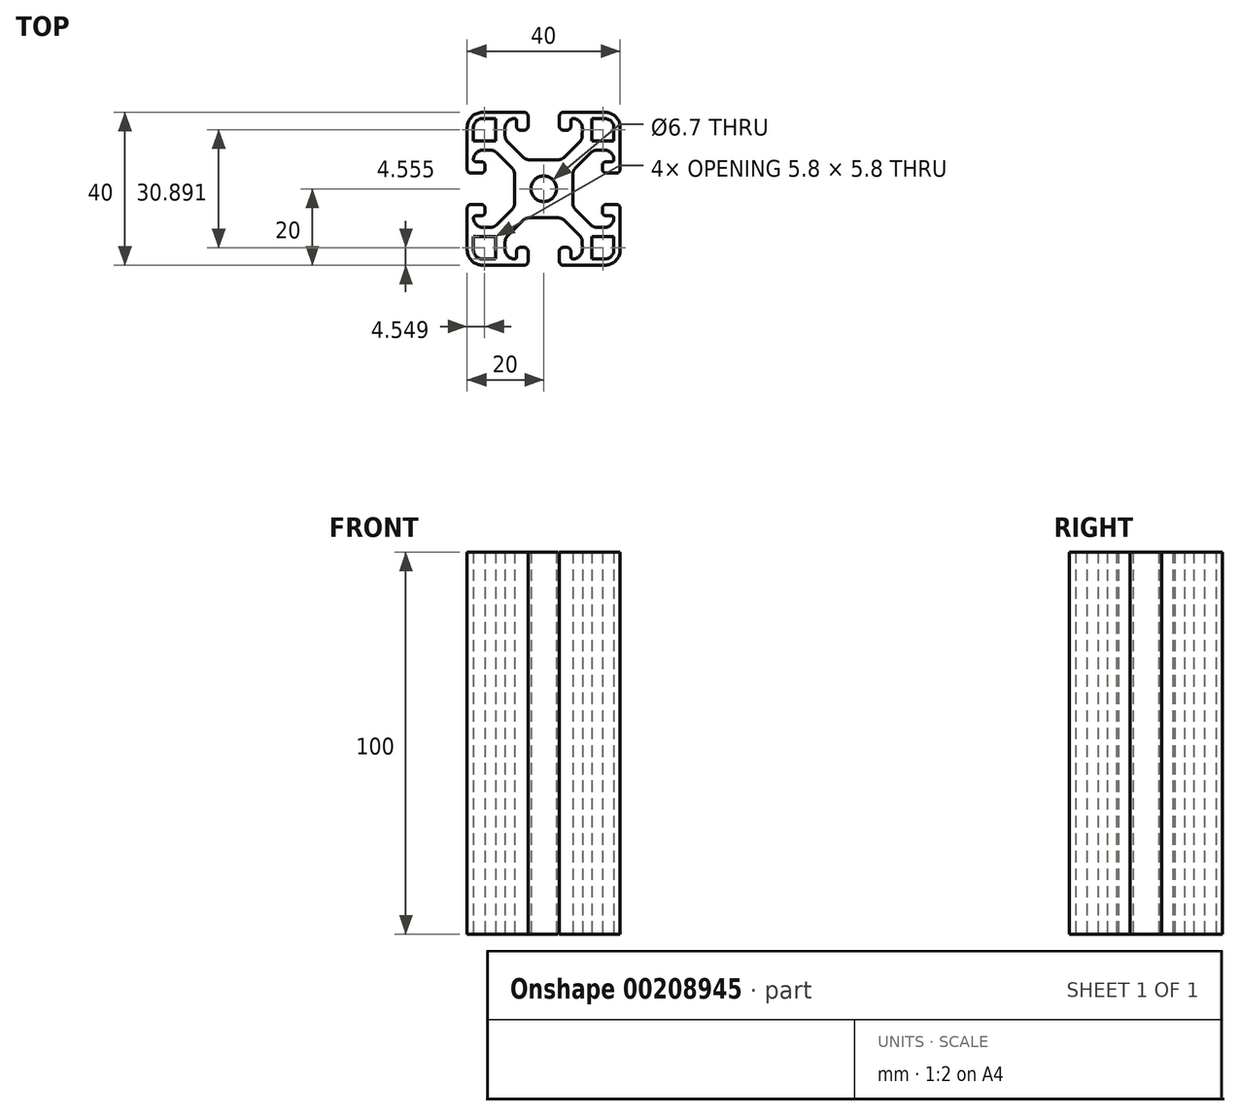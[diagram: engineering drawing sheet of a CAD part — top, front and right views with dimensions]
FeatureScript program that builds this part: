
annotation { "Feature Type Name" : "Feature", "Feature Type Description" : "" }
export const myFeature = defineFeature(function(context is Context, id is Id, definition is map)
    precondition{}
    {
        {
            var Q0;
            Q0=qCreatedBy(makeId("Top.planeOp"),FACE);
            var sketch = newSketch(context, id + "F0", { "sketchPlane" : qUnion([Q0])});
            skCircle(sketch, "E0", {"center": v(0, 0) * mm, "radius": 3.35 * mm});
            skPoint(sketch, "E1.rect.middle", {"position": v(13.8, 0) * mm});
            skPoint(sketch, "E2.newPointA", {"position": v(20, 20) * mm});
            skPoint(sketch, "E2.newPointB", {"position": v(20, -4.1) * mm});
            skArc(sketch, "E2.filletArc", {"start": v(20, -5.1) * mm, "mid": v(19.7, -4.4) * mm, "end": v(19, -4.1) * mm});
            skPoint(sketch, "E3.visualSharp", {"position": v(20, -20) * mm});
            skLineSegment(sketch, "E4", {"start": v(15.35, -5.1) * mm, "end": v(15.35, -6.1) * mm});
            skLineSegment(sketch, "E5", {"start": v(16.35, -7.1) * mm, "end": v(17.85, -7.1) * mm});
            skLineSegment(sketch, "E6", {"start": v(18.35, -7.6) * mm, "end": v(18.35, -7.6) * mm});
            skLineSegment(sketch, "E7", {"start": v(15.85, -10.1) * mm, "end": v(14, -10.1) * mm});
            skPoint(sketch, "E8.visualSharp", {"position": v(15.35, -4.1) * mm});
            skArc(sketch, "E8.filletArc", {"start": v(16.35, -4.1) * mm, "mid": v(15.64, -4.4) * mm, "end": v(15.35, -5.1) * mm});
            skPoint(sketch, "E9.visualSharp", {"position": v(15.35, -7.1) * mm});
            skArc(sketch, "E9.filletArc", {"start": v(15.35, -6.1) * mm, "mid": v(15.64, -6.8) * mm, "end": v(16.35, -7.1) * mm});
            skPoint(sketch, "E10.visualSharp", {"position": v(18.35, -7.1) * mm});
            skArc(sketch, "E10.filletArc", {"start": v(18.35, -7.6) * mm, "mid": v(18.2, -7.25) * mm, "end": v(17.85, -7.1) * mm});
            skPoint(sketch, "E11.visualSharp", {"position": v(18.35, -10.1) * mm});
            skArc(sketch, "E11.filletArc", {"start": v(15.85, -10.1) * mm, "mid": v(17.62, -9.37) * mm, "end": v(18.35, -7.6) * mm});
            skLineSegment(sketch, "E12", {"start": v(12.23, -9.37) * mm, "end": v(8.33, -5.48) * mm});
            skPoint(sketch, "E13.newPointA", {"position": v(7.6, -10.1) * mm});
            skArc(sketch, "E13.filletArc", {"start": v(12.23, -9.37) * mm, "mid": v(13.04, -9.9) * mm, "end": v(14, -10.1) * mm});
            skArc(sketch, "E14.filletArc", {"start": v(7.6, -3.7) * mm, "mid": v(7.8, -4.66) * mm, "end": v(8.33, -5.48) * mm});
            skArc(sketch, "E15.MirrorCS", {"start": v(9.37, -12.22) * mm, "mid": v(9.91, -13.03) * mm, "end": v(10.1, -13.99) * mm});
            skArc(sketch, "E16.MirrorCS", {"start": v(10.1, -15.85) * mm, "mid": v(9.37, -17.61) * mm, "end": v(7.6, -18.35) * mm});
            skLineSegment(sketch, "E17.MirrorCS", {"start": v(7.1, -16.35) * mm, "end": v(7.1, -17.85) * mm});
            skArc(sketch, "E18.MirrorCS", {"start": v(3.71, -7.6) * mm, "mid": v(4.67, -7.79) * mm, "end": v(5.48, -8.33) * mm});
            skArc(sketch, "E19.MirrorCS", {"start": v(5.1, -20) * mm, "mid": v(4.4, -19.7) * mm, "end": v(4.1, -19) * mm});
            skLineSegment(sketch, "E20.MirrorCS", {"start": v(10.1, -15.85) * mm, "end": v(10.1, -13.99) * mm});
            skArc(sketch, "E21.MirrorCS", {"start": v(6.1, -15.35) * mm, "mid": v(6.81, -15.64) * mm, "end": v(7.1, -16.35) * mm});
            skLineSegment(sketch, "E22.MirrorCS", {"start": v(9.37, -12.22) * mm, "end": v(5.48, -8.33) * mm});
            skLineSegment(sketch, "E23.MirrorCS", {"start": v(5.1, -15.35) * mm, "end": v(6.1, -15.35) * mm});
            skArc(sketch, "E24.MirrorCS", {"start": v(7.6, -18.35) * mm, "mid": v(7.25, -18.2) * mm, "end": v(7.1, -17.85) * mm});
            skLineSegment(sketch, "E25.MirrorCS", {"start": v(7.6, -18.35) * mm, "end": v(7.6, -18.35) * mm});
            skPoint(sketch, "E26.MirrorP", {"position": v(0, -13.8) * mm});
            skPoint(sketch, "E27.MirrorP", {"position": v(4.1, -15.35) * mm});
            skPoint(sketch, "E28.MirrorP", {"position": v(7.1, -15.35) * mm});
            skPoint(sketch, "E29.MirrorP", {"position": v(10.1, -18.35) * mm});
            skPoint(sketch, "E30.MirrorP", {"position": v(10.1, -7.6) * mm});
            skPoint(sketch, "E31.MirrorP", {"position": v(7.1, -18.35) * mm});
            skArc(sketch, "E32.MirrorCS", {"start": v(4.1, -16.35) * mm, "mid": v(4.4, -15.64) * mm, "end": v(5.1, -15.35) * mm});
            skLineSegment(sketch, "E33.bottom", {"start": v(16, -18.35) * mm, "end": v(12.55, -18.35) * mm});
            skLineSegment(sketch, "E33.top", {"start": v(18.35, -12.54) * mm, "end": v(12.55, -12.54) * mm});
            skLineSegment(sketch, "E33.left", {"start": v(18.35, -16) * mm, "end": v(18.35, -12.54) * mm});
            skLineSegment(sketch, "E33.right", {"start": v(12.55, -18.35) * mm, "end": v(12.55, -12.54) * mm});
            skPoint(sketch, "E34.visualSharp", {"position": v(18.35, -18.35) * mm});
            skArc(sketch, "E34.filletArc", {"start": v(16, -18.35) * mm, "mid": v(17.66, -17.66) * mm, "end": v(18.35, -16) * mm});
            skLineSegment(sketch, "E35.MirrorCS", {"start": v(-18.35, -7.6) * mm, "end": v(-18.35, -7.6) * mm});
            skPoint(sketch, "E36.MirrorP", {"position": v(-18.35, -10.1) * mm});
            skPoint(sketch, "E37.MirrorP", {"position": v(-18.35, -18.35) * mm});
            skArc(sketch, "E38.MirrorCS", {"start": v(-15.85, -10.1) * mm, "mid": v(-17.62, -9.37) * mm, "end": v(-18.35, -7.6) * mm});
            skPoint(sketch, "E39.MirrorP", {"position": v(-13.8, 0) * mm});
            skArc(sketch, "E40.MirrorCS", {"start": v(-6.1, -15.35) * mm, "mid": v(-6.81, -15.64) * mm, "end": v(-7.1, -16.35) * mm});
            skLineSegment(sketch, "E41.MirrorCS", {"start": v(-16.35, -7.1) * mm, "end": v(-17.85, -7.1) * mm});
            skLineSegment(sketch, "E42.MirrorCS", {"start": v(-15.85, -10.1) * mm, "end": v(-14, -10.1) * mm});
            skPoint(sketch, "E43.MirrorP", {"position": v(-18.35, -7.1) * mm});
            skArc(sketch, "E44.MirrorCS", {"start": v(-20, -5.1) * mm, "mid": v(-19.7, -4.4) * mm, "end": v(-19, -4.1) * mm});
            skLineSegment(sketch, "E45.MirrorCS", {"start": v(-15.35, -5.1) * mm, "end": v(-15.35, -6.1) * mm});
            skPoint(sketch, "E46.MirrorP", {"position": v(-15.35, -4.1) * mm});
            skLineSegment(sketch, "E47.MirrorCS", {"start": v(-7.1, -16.35) * mm, "end": v(-7.1, -17.85) * mm});
            skPoint(sketch, "E48.MirrorP", {"position": v(-20, -20) * mm});
            skPoint(sketch, "E49.MirrorP", {"position": v(-15.35, -7.1) * mm});
            skPoint(sketch, "E50.MirrorP", {"position": v(-20, -4.1) * mm});
            skLineSegment(sketch, "E51.MirrorCS", {"start": v(-7.6, -18.35) * mm, "end": v(-7.6, -18.35) * mm});
            skPoint(sketch, "E52.MirrorP", {"position": v(-10.1, -7.6) * mm});
            skArc(sketch, "E53.MirrorCS", {"start": v(-7.6, -18.35) * mm, "mid": v(-7.25, -18.2) * mm, "end": v(-7.1, -17.85) * mm});
            skLineSegment(sketch, "E54.MirrorCS", {"start": v(-18.35, -16) * mm, "end": v(-18.35, -12.54) * mm});
            skArc(sketch, "E55.MirrorCS", {"start": v(-15.35, -6.1) * mm, "mid": v(-15.64, -6.8) * mm, "end": v(-16.35, -7.1) * mm});
            skArc(sketch, "E56.MirrorCS", {"start": v(-18.35, -7.6) * mm, "mid": v(-18.2, -7.25) * mm, "end": v(-17.85, -7.1) * mm});
            skPoint(sketch, "E57.MirrorP", {"position": v(-7.1, -15.35) * mm});
            skPoint(sketch, "E58.MirrorP", {"position": v(-7.6, -10.1) * mm});
            skLineSegment(sketch, "E59.MirrorCS", {"start": v(-12.55, -18.35) * mm, "end": v(-12.55, -12.54) * mm});
            skArc(sketch, "E60.MirrorCS", {"start": v(-16.35, -4.1) * mm, "mid": v(-15.64, -4.4) * mm, "end": v(-15.35, -5.1) * mm});
            skArc(sketch, "E61.MirrorCS", {"start": v(-12.23, -9.37) * mm, "mid": v(-13.04, -9.9) * mm, "end": v(-14, -10.1) * mm});
            skArc(sketch, "E62.MirrorCS", {"start": v(-9.37, -12.22) * mm, "mid": v(-9.91, -13.03) * mm, "end": v(-10.1, -13.99) * mm});
            skPoint(sketch, "E63.MirrorP", {"position": v(-4.1, -15.35) * mm});
            skLineSegment(sketch, "E64.MirrorCS", {"start": v(-18.35, -12.54) * mm, "end": v(-12.55, -12.54) * mm});
            skArc(sketch, "E65.MirrorCS", {"start": v(-7.6, -3.7) * mm, "mid": v(-7.8, -4.66) * mm, "end": v(-8.33, -5.48) * mm});
            skPoint(sketch, "E66.MirrorP", {"position": v(-7.1, -18.35) * mm});
            skArc(sketch, "E67.MirrorCS", {"start": v(-4.1, -16.35) * mm, "mid": v(-4.4, -15.64) * mm, "end": v(-5.1, -15.35) * mm});
            skLineSegment(sketch, "E68.MirrorCS", {"start": v(-9.37, -12.22) * mm, "end": v(-5.48, -8.33) * mm});
            skLineSegment(sketch, "E69.MirrorCS", {"start": v(-10.1, -15.85) * mm, "end": v(-10.1, -13.99) * mm});
            skArc(sketch, "E70.MirrorCS", {"start": v(-5.1, -20) * mm, "mid": v(-4.4, -19.7) * mm, "end": v(-4.1, -19) * mm});
            skPoint(sketch, "E71.MirrorP", {"position": v(-10.1, -18.35) * mm});
            skPoint(sketch, "E72.MirrorP", {"position": v(-4.1, -20) * mm});
            skArc(sketch, "E73.MirrorCS", {"start": v(-16, -18.35) * mm, "mid": v(-17.66, -17.66) * mm, "end": v(-18.35, -16) * mm});
            skLineSegment(sketch, "E74.MirrorCS", {"start": v(-16, -18.35) * mm, "end": v(-12.55, -18.35) * mm});
            skArc(sketch, "E75.MirrorCS", {"start": v(-10.1, -15.85) * mm, "mid": v(-9.37, -17.61) * mm, "end": v(-7.6, -18.35) * mm});
            skArc(sketch, "E76.MirrorCS", {"start": v(-3.71, -7.6) * mm, "mid": v(-4.67, -7.79) * mm, "end": v(-5.48, -8.33) * mm});
            skLineSegment(sketch, "E77.MirrorCS", {"start": v(-5.1, -15.35) * mm, "end": v(-6.1, -15.35) * mm});
            skLineSegment(sketch, "E78.MirrorCS", {"start": v(-12.23, -9.37) * mm, "end": v(-8.33, -5.48) * mm});
            skLineSegment(sketch, "E79.MirrorCS", {"start": v(-12.23, 9.37) * mm, "end": v(-8.33, 5.48) * mm});
            skArc(sketch, "E80.MirrorCS", {"start": v(16, 18.35) * mm, "mid": v(17.66, 17.66) * mm, "end": v(18.35, 16) * mm});
            skArc(sketch, "E81.MirrorCS", {"start": v(10.1, 15.85) * mm, "mid": v(9.37, 17.61) * mm, "end": v(7.6, 18.35) * mm});
            skLineSegment(sketch, "E82.MirrorCS", {"start": v(-15.35, 5.1) * mm, "end": v(-15.35, 6.1) * mm});
            skLineSegment(sketch, "E83.MirrorCS", {"start": v(5.1, 15.35) * mm, "end": v(6.1, 15.35) * mm});
            skArc(sketch, "E84.MirrorCS", {"start": v(-6.1, 15.35) * mm, "mid": v(-6.81, 15.64) * mm, "end": v(-7.1, 16.35) * mm});
            skLineSegment(sketch, "E85.MirrorCS", {"start": v(7.1, 16.35) * mm, "end": v(7.1, 17.85) * mm});
            skLineSegment(sketch, "E86.MirrorCS", {"start": v(-12.55, 18.35) * mm, "end": v(-12.55, 12.54) * mm});
            skLineSegment(sketch, "E87.MirrorCS", {"start": v(12.23, 9.37) * mm, "end": v(8.33, 5.48) * mm});
            skLineSegment(sketch, "E88.MirrorCS", {"start": v(-7.1, 16.35) * mm, "end": v(-7.1, 17.85) * mm});
            skArc(sketch, "E89.MirrorCS", {"start": v(-12.23, 9.37) * mm, "mid": v(-13.04, 9.9) * mm, "end": v(-14, 10.1) * mm});
            skArc(sketch, "E90.MirrorCS", {"start": v(-3.71, 7.6) * mm, "mid": v(-4.67, 7.79) * mm, "end": v(-5.48, 8.33) * mm});
            skArc(sketch, "E91.MirrorCS", {"start": v(12.23, 9.37) * mm, "mid": v(13.04, 9.9) * mm, "end": v(14, 10.1) * mm});
            skArc(sketch, "E92.MirrorCS", {"start": v(7.6, 18.35) * mm, "mid": v(7.25, 18.2) * mm, "end": v(7.1, 17.85) * mm});
            skArc(sketch, "E93.MirrorCS", {"start": v(5.1, 20) * mm, "mid": v(4.4, 19.7) * mm, "end": v(4.1, 19) * mm});
            skArc(sketch, "E94.MirrorCS", {"start": v(-4.1, 16.35) * mm, "mid": v(-4.4, 15.64) * mm, "end": v(-5.1, 15.35) * mm});
            skLineSegment(sketch, "E95.MirrorCS", {"start": v(-5.1, 15.35) * mm, "end": v(-6.1, 15.35) * mm});
            skArc(sketch, "E96.MirrorCS", {"start": v(3.71, 7.6) * mm, "mid": v(4.67, 7.79) * mm, "end": v(5.48, 8.33) * mm});
            skArc(sketch, "E97.MirrorCS", {"start": v(4.1, 16.35) * mm, "mid": v(4.4, 15.64) * mm, "end": v(5.1, 15.35) * mm});
            skArc(sketch, "E98.MirrorCS", {"start": v(-7.6, 18.35) * mm, "mid": v(-7.25, 18.2) * mm, "end": v(-7.1, 17.85) * mm});
            skArc(sketch, "E99.MirrorCS", {"start": v(7.6, 3.7) * mm, "mid": v(7.8, 4.66) * mm, "end": v(8.33, 5.48) * mm});
            skArc(sketch, "E100.MirrorCS", {"start": v(-16.35, 4.1) * mm, "mid": v(-15.64, 4.4) * mm, "end": v(-15.35, 5.1) * mm});
            skArc(sketch, "E101.MirrorCS", {"start": v(-16, 18.35) * mm, "mid": v(-17.66, 17.66) * mm, "end": v(-18.35, 16) * mm});
            skArc(sketch, "E102.MirrorCS", {"start": v(-9.37, 12.22) * mm, "mid": v(-9.91, 13.03) * mm, "end": v(-10.1, 13.99) * mm});
            skArc(sketch, "E103.MirrorCS", {"start": v(-10.1, 15.85) * mm, "mid": v(-9.37, 17.61) * mm, "end": v(-7.6, 18.35) * mm});
            skArc(sketch, "E104.MirrorCS", {"start": v(-15.85, 10.1) * mm, "mid": v(-17.62, 9.37) * mm, "end": v(-18.35, 7.6) * mm});
            skLineSegment(sketch, "E105.MirrorCS", {"start": v(16, 18.35) * mm, "end": v(12.55, 18.35) * mm});
            skLineSegment(sketch, "E106.MirrorCS", {"start": v(-15.85, 10.1) * mm, "end": v(-14, 10.1) * mm});
            skArc(sketch, "E107.MirrorCS", {"start": v(-7.6, 3.7) * mm, "mid": v(-7.8, 4.66) * mm, "end": v(-8.33, 5.48) * mm});
            skLineSegment(sketch, "E108.MirrorCS", {"start": v(-16, 18.35) * mm, "end": v(-12.55, 18.35) * mm});
            skLineSegment(sketch, "E109.MirrorCS", {"start": v(-16.35, 7.1) * mm, "end": v(-17.85, 7.1) * mm});
            skLineSegment(sketch, "E110.MirrorCS", {"start": v(15.85, 10.1) * mm, "end": v(14, 10.1) * mm});
            skLineSegment(sketch, "E111.MirrorCS", {"start": v(10.1, 15.85) * mm, "end": v(10.1, 13.99) * mm});
            skLineSegment(sketch, "E112.MirrorCS", {"start": v(-18.35, 16) * mm, "end": v(-18.35, 12.54) * mm});
            skArc(sketch, "E113.MirrorCS", {"start": v(16.35, 4.1) * mm, "mid": v(15.64, 4.4) * mm, "end": v(15.35, 5.1) * mm});
            skLineSegment(sketch, "E114.MirrorCS", {"start": v(15.35, 5.1) * mm, "end": v(15.35, 6.1) * mm});
            skLineSegment(sketch, "E115.MirrorCS", {"start": v(18.35, 12.54) * mm, "end": v(12.55, 12.54) * mm});
            skArc(sketch, "E116.MirrorCS", {"start": v(20, 5.1) * mm, "mid": v(19.7, 4.4) * mm, "end": v(19, 4.1) * mm});
            skArc(sketch, "E117.MirrorCS", {"start": v(9.37, 12.22) * mm, "mid": v(9.91, 13.03) * mm, "end": v(10.1, 13.99) * mm});
            skLineSegment(sketch, "E118.MirrorCS", {"start": v(-18.35, 12.54) * mm, "end": v(-12.55, 12.54) * mm});
            skArc(sketch, "E119.MirrorCS", {"start": v(15.35, 6.1) * mm, "mid": v(15.64, 6.8) * mm, "end": v(16.35, 7.1) * mm});
            skLineSegment(sketch, "E120.MirrorCS", {"start": v(-9.37, 12.22) * mm, "end": v(-5.48, 8.33) * mm});
            skLineSegment(sketch, "E121.MirrorCS", {"start": v(18.35, 16) * mm, "end": v(18.35, 12.54) * mm});
            skArc(sketch, "E122.MirrorCS", {"start": v(-15.35, 6.1) * mm, "mid": v(-15.64, 6.8) * mm, "end": v(-16.35, 7.1) * mm});
            skLineSegment(sketch, "E123.MirrorCS", {"start": v(18.35, 7.6) * mm, "end": v(18.35, 7.6) * mm});
            skPoint(sketch, "E124.MirrorP", {"position": v(0, 13.8) * mm});
            skLineSegment(sketch, "E125.MirrorCS", {"start": v(7.6, 18.35) * mm, "end": v(7.6, 18.35) * mm});
            skPoint(sketch, "E126.MirrorP", {"position": v(18.35, 10.1) * mm});
            skPoint(sketch, "E127.MirrorP", {"position": v(10.1, 7.6) * mm});
            skPoint(sketch, "E128.MirrorP", {"position": v(20, 4.1) * mm});
            skArc(sketch, "E129.MirrorCS", {"start": v(18.35, 7.6) * mm, "mid": v(18.2, 7.25) * mm, "end": v(17.85, 7.1) * mm});
            skPoint(sketch, "E130.MirrorP", {"position": v(10.1, 18.35) * mm});
            skPoint(sketch, "E131.MirrorP", {"position": v(18.35, 7.1) * mm});
            skPoint(sketch, "E132.MirrorP", {"position": v(7.1, 15.35) * mm});
            skPoint(sketch, "E133.MirrorP", {"position": v(4.1, 15.35) * mm});
            skPoint(sketch, "E134.MirrorP", {"position": v(15.35, 4.1) * mm});
            skPoint(sketch, "E135.MirrorP", {"position": v(7.6, 10.1) * mm});
            skPoint(sketch, "E136.MirrorP", {"position": v(7.1, 18.35) * mm});
            skPoint(sketch, "E137.MirrorP", {"position": v(15.35, 7.1) * mm});
            skPoint(sketch, "E138.MirrorP", {"position": v(4.1, 20) * mm});
            skPoint(sketch, "E139.MirrorP", {"position": v(18.35, 18.35) * mm});
            skArc(sketch, "E140.MirrorCS", {"start": v(15.85, 10.1) * mm, "mid": v(17.62, 9.37) * mm, "end": v(18.35, 7.6) * mm});
            skPoint(sketch, "E141.MirrorP", {"position": v(-4.1, 20) * mm});
            skLineSegment(sketch, "E142.MirrorCS", {"start": v(12.55, 18.35) * mm, "end": v(12.55, 12.54) * mm});
            skArc(sketch, "E143.MirrorCS", {"start": v(6.1, 15.35) * mm, "mid": v(6.81, 15.64) * mm, "end": v(7.1, 16.35) * mm});
            skLineSegment(sketch, "E144.MirrorCS", {"start": v(-10.1, 15.85) * mm, "end": v(-10.1, 13.99) * mm});
            skPoint(sketch, "E145.MirrorP", {"position": v(-4.1, 15.35) * mm});
            skLineSegment(sketch, "E146.MirrorCS", {"start": v(-7.6, 18.35) * mm, "end": v(-7.6, 18.35) * mm});
            skLineSegment(sketch, "E147.MirrorCS", {"start": v(9.37, 12.22) * mm, "end": v(5.48, 8.33) * mm});
            skPoint(sketch, "E148.MirrorP", {"position": v(-10.1, 7.6) * mm});
            skArc(sketch, "E149.MirrorCS", {"start": v(-20, 5.1) * mm, "mid": v(-19.7, 4.4) * mm, "end": v(-19, 4.1) * mm});
            skPoint(sketch, "E150.MirrorP", {"position": v(-10.1, 18.35) * mm});
            skPoint(sketch, "E151.MirrorP", {"position": v(-7.6, 10.1) * mm});
            skPoint(sketch, "E152.MirrorP", {"position": v(-7.1, 15.35) * mm});
            skLineSegment(sketch, "E153.MirrorCS", {"start": v(-18.35, 7.6) * mm, "end": v(-18.35, 7.6) * mm});
            skPoint(sketch, "E154.MirrorP", {"position": v(-7.1, 18.35) * mm});
            skArc(sketch, "E155.MirrorCS", {"start": v(-5.1, 20) * mm, "mid": v(-4.4, 19.7) * mm, "end": v(-4.1, 19) * mm});
            skArc(sketch, "E156.MirrorCS", {"start": v(-18.35, 7.6) * mm, "mid": v(-18.2, 7.25) * mm, "end": v(-17.85, 7.1) * mm});
            skPoint(sketch, "E157.MirrorP", {"position": v(-18.35, 18.35) * mm});
            skPoint(sketch, "E158.MirrorP", {"position": v(-15.35, 7.1) * mm});
            skPoint(sketch, "E159.MirrorP", {"position": v(-18.35, 10.1) * mm});
            skPoint(sketch, "E160.MirrorP", {"position": v(-18.35, 7.1) * mm});
            skPoint(sketch, "E161.MirrorP", {"position": v(-15.35, 4.1) * mm});
            skPoint(sketch, "E162.MirrorP", {"position": v(-20, 4.1) * mm});
            skPoint(sketch, "E163.MirrorP", {"position": v(-20, 20) * mm});
            skLineSegment(sketch, "E164", {"start": v(-19, -4.1) * mm, "end": v(-16.35, -4.1) * mm});
            skLineSegment(sketch, "E165", {"start": v(-4.1, -16.35) * mm, "end": v(-4.1, -19) * mm});
            skLineSegment(sketch, "E166", {"start": v(4.1, -16.35) * mm, "end": v(4.1, -19) * mm});
            skLineSegment(sketch, "E167", {"start": v(16.35, -4.1) * mm, "end": v(19, -4.1) * mm});
            skLineSegment(sketch, "E168", {"start": v(-19, 4.1) * mm, "end": v(-16.35, 4.1) * mm});
            skLineSegment(sketch, "E169", {"start": v(-4.1, 19) * mm, "end": v(-4.1, 16.35) * mm});
            skLineSegment(sketch, "E170", {"start": v(4.1, 19) * mm, "end": v(4.1, 16.35) * mm});
            skLineSegment(sketch, "E171", {"start": v(16.35, 7.1) * mm, "end": v(17.85, 7.1) * mm});
            skLineSegment(sketch, "E172", {"start": v(16.35, 4.1) * mm, "end": v(19, 4.1) * mm});
            skLineSegment(sketch, "E173", {"start": v(7.6, 3.7) * mm, "end": v(7.6, -3.7) * mm});
            skLineSegment(sketch, "E174", {"start": v(-3.71, 7.6) * mm, "end": v(3.71, 7.6) * mm});
            skLineSegment(sketch, "E175", {"start": v(-7.6, 3.7) * mm, "end": v(-7.6, -3.7) * mm});
            skLineSegment(sketch, "E176", {"start": v(-3.71, -7.6) * mm, "end": v(3.71, -7.6) * mm});
            skLineSegment(sketch, "E177", {"start": v(-20, -5.1) * mm, "end": v(-20, -16) * mm});
            skLineSegment(sketch, "E178", {"start": v(-5.1, -20) * mm, "end": v(-16, -20) * mm});
            skLineSegment(sketch, "E179", {"start": v(-20, 5.1) * mm, "end": v(-20, 16) * mm});
            skLineSegment(sketch, "E180", {"start": v(-5.1, 20) * mm, "end": v(-16, 20) * mm});
            skLineSegment(sketch, "E181", {"start": v(20, -5.1) * mm, "end": v(20, -16) * mm});
            skLineSegment(sketch, "E182", {"start": v(5.1, -20) * mm, "end": v(16, -20) * mm});
            skLineSegment(sketch, "E183", {"start": v(16, 20) * mm, "end": v(5.1, 20) * mm});
            skLineSegment(sketch, "E184", {"start": v(20, 5.1) * mm, "end": v(20, 16) * mm});
            skArc(sketch, "E185.filletArc", {"start": v(20, 16) * mm, "mid": v(18.83, 18.83) * mm, "end": v(16, 20) * mm});
            skArc(sketch, "E186.filletArc", {"start": v(-16, 20) * mm, "mid": v(-18.83, 18.82) * mm, "end": v(-20, 16) * mm});
            skArc(sketch, "E187.filletArc", {"start": v(-20, -16) * mm, "mid": v(-18.83, -18.82) * mm, "end": v(-16, -20) * mm});
            skArc(sketch, "E188.filletArc", {"start": v(16, -20) * mm, "mid": v(18.83, -18.82) * mm, "end": v(20, -16) * mm});
            skSolve(sketch);
        }
        {
            var Q0;
            Q0=makeQuery(id+"F0.imprint","IMPRINT",FACE,{"disambiguationData":[TD([[makeQuery(id+"F0.imprint","IMPRINT",EDGE,{"derivedFrom":sQuery(id+"F0.wireOp",EDGE,"E2.filletArc")}),1.0]])]});
            extrude(context, id + "F1", {"entities" : qUnion([Q0]), "depth" : 100 * mm});
        }
    });
